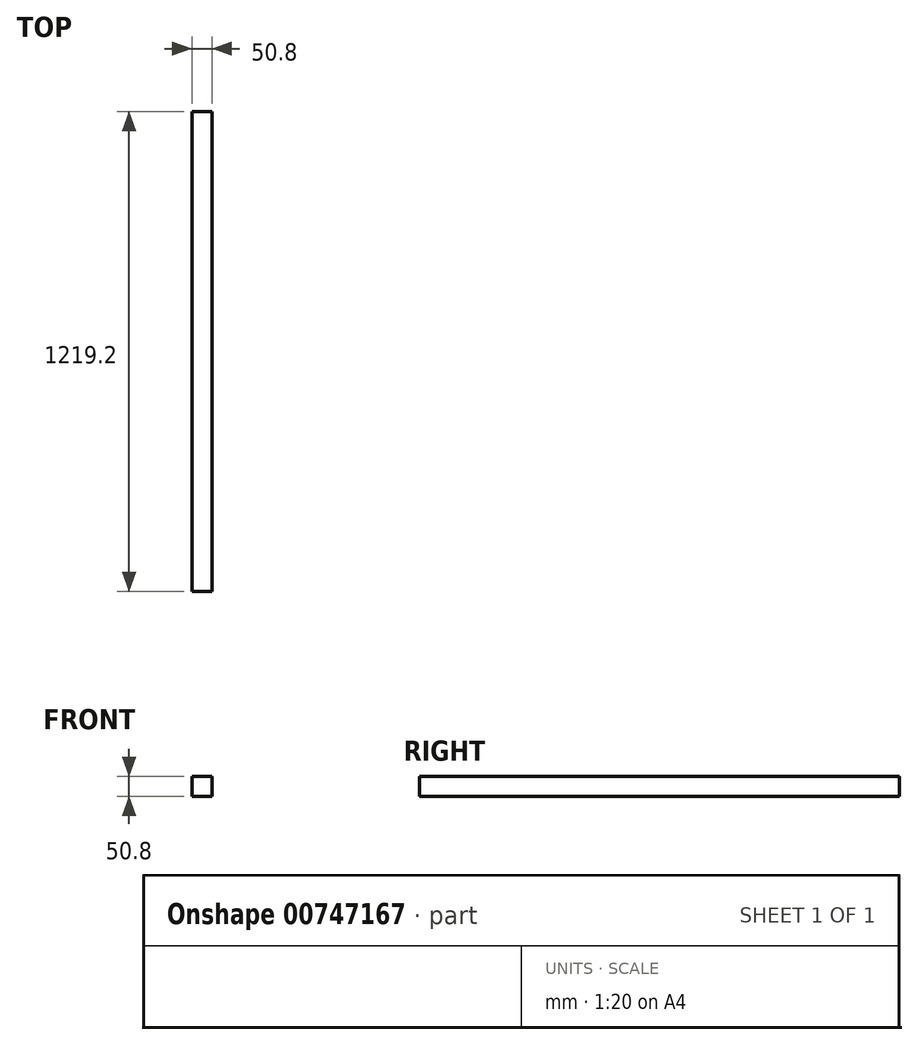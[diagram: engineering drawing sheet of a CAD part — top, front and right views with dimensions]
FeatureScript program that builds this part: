
annotation { "Feature Type Name" : "Feature", "Feature Type Description" : "" }
export const myFeature = defineFeature(function(context is Context, id is Id, definition is map)
    precondition{}
    {
        {
            var Q0;
            Q0=qCreatedBy(makeId("Front.planeOp"),FACE);
            var sketch = newSketch(context, id + "F0", { "sketchPlane" : qUnion([Q0])});
            skLineSegment(sketch, "E0.bottom", {"start": v(-84.27, 58) * mm, "end": v(-33.47, 58) * mm});
            skLineSegment(sketch, "E0.top", {"start": v(-84.27, 7.2) * mm, "end": v(-33.47, 7.2) * mm});
            skLineSegment(sketch, "E0.left", {"start": v(-84.27, 58) * mm, "end": v(-84.27, 7.2) * mm});
            skLineSegment(sketch, "E0.right", {"start": v(-33.47, 58) * mm, "end": v(-33.47, 7.2) * mm});
            skSolve(sketch);
        }
        {
            var Q0;
            Q0 = qSketchRegion(id + "F0", true);
            extrude(context, id + "F1", {"entities" : qUnion([Q0]), "depth" : 1219.2 * mm, "offsetDistance" : 25.4 * mm});
        }
    });
